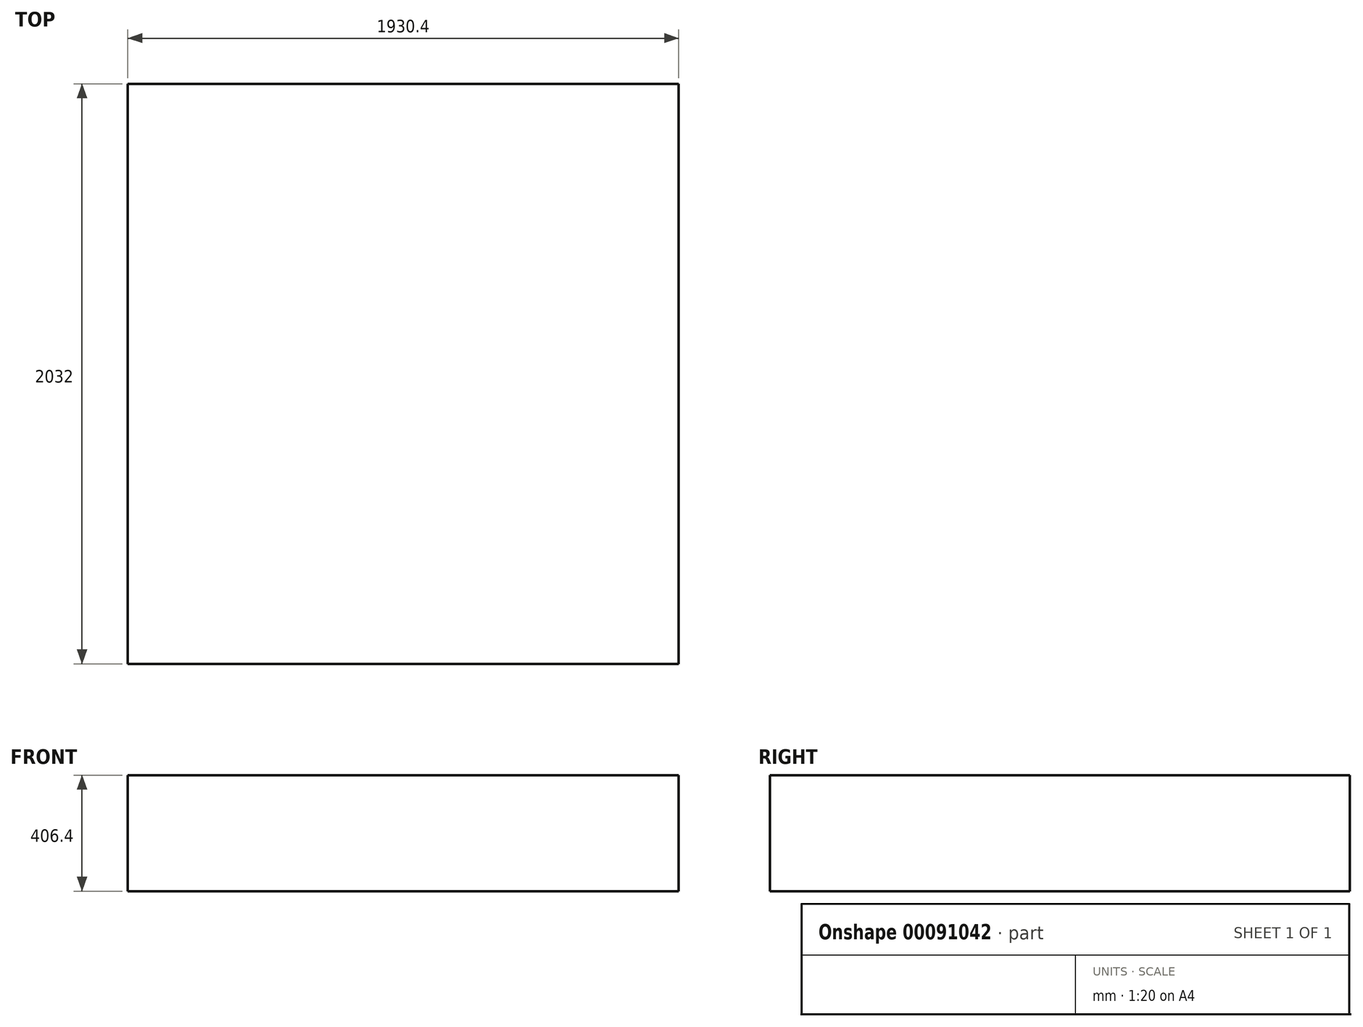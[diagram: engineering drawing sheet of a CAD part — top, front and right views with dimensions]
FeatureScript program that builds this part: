
annotation { "Feature Type Name" : "Feature", "Feature Type Description" : "" }
export const myFeature = defineFeature(function(context is Context, id is Id, definition is map)
    precondition{}
    {
        {
            var Q0;
            Q0=qCreatedBy(makeId("Top.planeOp"),FACE);
            var sketch = newSketch(context, id + "F0", { "sketchPlane" : qUnion([Q0])});
            skLineSegment(sketch, "E0.bottom", {"start": v(-958.5, 898.18) * mm, "end": v(971.9, 898.18) * mm});
            skLineSegment(sketch, "E0.top", {"start": v(-958.5, -1133.82) * mm, "end": v(971.9, -1133.82) * mm});
            skLineSegment(sketch, "E0.left", {"start": v(-958.5, 898.18) * mm, "end": v(-958.5, -1133.82) * mm});
            skLineSegment(sketch, "E0.right", {"start": v(971.9, 898.18) * mm, "end": v(971.9, -1133.82) * mm});
            skSolve(sketch);
        }
        {
            var Q0;
            Q0 = qSketchRegion(id + "F0", true);
            extrude(context, id + "F1", {"entities" : qUnion([Q0]), "depth" : 406.4 * mm});
        }
    });
